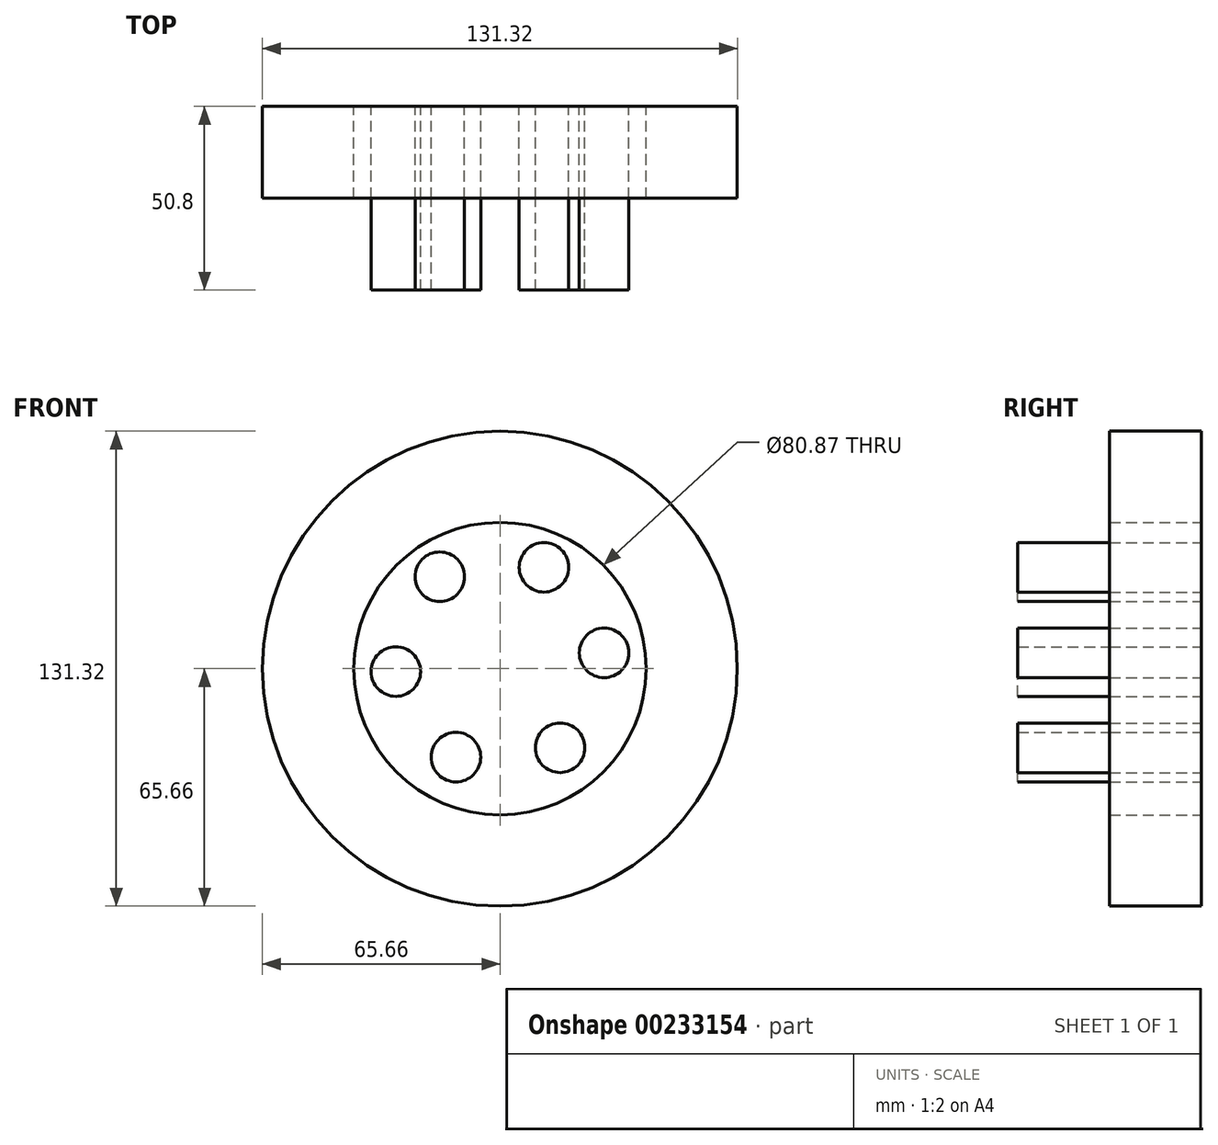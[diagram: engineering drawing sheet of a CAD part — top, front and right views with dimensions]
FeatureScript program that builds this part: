
annotation { "Feature Type Name" : "Feature", "Feature Type Description" : "" }
export const myFeature = defineFeature(function(context is Context, id is Id, definition is map)
    precondition{}
    {
        {
            var Q0;
            Q0=qCreatedBy(makeId("Front.planeOp"),FACE);
            var sketch = newSketch(context, id + "F0", { "sketchPlane" : qUnion([Q0])});
            skCircle(sketch, "E0", {"center": v(0, 0) * mm, "radius": 65.66 * mm});
            skCircle(sketch, "E1", {"center": v(0, 0) * mm, "radius": 40.44 * mm});
            skCircle(sketch, "E2", {"center": v(0, 27.91) * mm, "radius": 7.4 * mm});
            skCircle(sketch, "E3.1.0", {"center": v(-24.17, 13.96) * mm, "radius": 7.4 * mm});
            skCircle(sketch, "E3.2.0", {"center": v(-24.17, -13.96) * mm, "radius": 7.4 * mm});
            skCircle(sketch, "E3.3.0", {"center": v(0, -27.91) * mm, "radius": 7.4 * mm});
            skCircle(sketch, "E3.4.0", {"center": v(24.17, -13.96) * mm, "radius": 7.4 * mm});
            skCircle(sketch, "E3.5.0", {"center": v(24.17, 13.96) * mm, "radius": 7.4 * mm});
            skSolve(sketch);
        }
        {
            var Q0;
            Q0=qCreatedBy(makeId("Front.planeOp"),FACE);
            var sketch = newSketch(context, id + "F1", { "sketchPlane" : qUnion([Q0])});
            skCircle(sketch, "E4", {"center": v(0, 0) * mm, "radius": 67.87 * mm});
            skSolve(sketch);
        }
        {
            var Q0;
            Q0=sQuery(id+"F1.wireOp",EDGE,"E4");
            extrude(context, id + "F2", {"bodyType" : ToolBodyType.SURFACE, "surfaceEntities" : qUnion([Q0]), "depth" : 25.4 * mm});
        }
        {
            var Q0;
            Q0 = qSketchRegion(id + "F0", true);
            extrude(context, id + "F3", {"entities" : qUnion([Q0]), "depth" : 25.4 * mm});
        }
        {
            var Q0;
            Q0=qCreatedBy(makeId("Front.planeOp"),FACE);
            var sketch = newSketch(context, id + "F4", { "sketchPlane" : qUnion([Q0])});
            skCircle(sketch, "E5", {"center": v(-16.64, 25.43) * mm, "radius": 6.85 * mm});
            skCircle(sketch, "E6.1.0", {"center": v(-28.8, -0.8) * mm, "radius": 6.85 * mm});
            skCircle(sketch, "E6.2.0", {"center": v(-12.16, -24.46) * mm, "radius": 6.85 * mm});
            skCircle(sketch, "E6.3.0", {"center": v(16.64, -21.87) * mm, "radius": 6.85 * mm});
            skCircle(sketch, "E6.4.0", {"center": v(28.8, 4.37) * mm, "radius": 6.85 * mm});
            skCircle(sketch, "E6.5.0", {"center": v(12.16, 28.02) * mm, "radius": 6.85 * mm});
            skPoint(sketch, "E6.center", {"position": v(0, 1.78) * mm});
            skSolve(sketch);
        }
        {
            var Q0;
            Q0=makeQuery(id+"F4.imprint","IMPRINT",FACE,{"disambiguationData":[TD([[makeQuery(id+"F4.imprint","IMPRINT",EDGE,{"derivedFrom":sQuery(id+"F4.wireOp",EDGE,"E6.5.0")}),1.0]])]});
            var Q1;
            Q1=makeQuery(id+"F4.imprint","IMPRINT",FACE,{"disambiguationData":[TD([[makeQuery(id+"F4.imprint","IMPRINT",EDGE,{"derivedFrom":sQuery(id+"F4.wireOp",EDGE,"E5")}),1.0]])]});
            var Q2;
            Q2=makeQuery(id+"F4.imprint","IMPRINT",FACE,{"disambiguationData":[TD([[makeQuery(id+"F4.imprint","IMPRINT",EDGE,{"derivedFrom":sQuery(id+"F4.wireOp",EDGE,"E6.1.0")}),1.0]])]});
            var Q3;
            Q3=makeQuery(id+"F4.imprint","IMPRINT",FACE,{"disambiguationData":[TD([[makeQuery(id+"F4.imprint","IMPRINT",EDGE,{"derivedFrom":sQuery(id+"F4.wireOp",EDGE,"E6.2.0")}),1.0]])]});
            var Q4;
            Q4=makeQuery(id+"F4.imprint","IMPRINT",FACE,{"disambiguationData":[TD([[makeQuery(id+"F4.imprint","IMPRINT",EDGE,{"derivedFrom":sQuery(id+"F4.wireOp",EDGE,"E6.3.0")}),1.0]])]});
            var Q5;
            Q5=makeQuery(id+"F4.imprint","IMPRINT",FACE,{"disambiguationData":[TD([[makeQuery(id+"F4.imprint","IMPRINT",EDGE,{"derivedFrom":sQuery(id+"F4.wireOp",EDGE,"E6.4.0")}),1.0]])]});
            extrude(context, id + "F5", {"entities" : qUnion([Q0, Q1, Q2, Q3, Q4, Q5]), "depth" : 25.4 * mm});
        }
        {
            var Q0;
            Q0=makeQuery(id+"F5.opExtrude","CAP_FACE",FACE,{"disambiguationData":[OSD([sQuery(id+"F4.wireOp",EDGE,"E6.2.0")])],"isStart":false});
            var Q1;
            Q1=makeQuery(id+"F5.opExtrude","CAP_FACE",FACE,{"disambiguationData":[OSD([sQuery(id+"F4.wireOp",EDGE,"E6.3.0")])],"isStart":false});
            var Q2;
            Q2=makeQuery(id+"F5.opExtrude","CAP_FACE",FACE,{"disambiguationData":[OSD([sQuery(id+"F4.wireOp",EDGE,"E6.4.0")])],"isStart":false});
            var Q3;
            Q3=makeQuery(id+"F5.opExtrude","CAP_FACE",FACE,{"disambiguationData":[OSD([sQuery(id+"F4.wireOp",EDGE,"E6.1.0")])],"isStart":false});
            extrude(context, id + "F6", {"entities" : qUnion([Q0, Q1, Q2, Q3]), "depth" : 25.4 * mm});
        }
        {
            var Q0;
            Q0=makeQuery(id+"F5.opExtrude","CAP_FACE",FACE,{"disambiguationData":[OSD([sQuery(id+"F4.wireOp",EDGE,"E5")])],"isStart":false});
            extrude(context, id + "F7", {"entities" : qUnion([Q0]), "operationType" : NewBodyOperationType.ADD, "depth" : 25.4 * mm});
        }
        {
            var Q0;
            Q0=makeQuery(id+"F5.opExtrude","CAP_FACE",FACE,{"disambiguationData":[OSD([sQuery(id+"F4.wireOp",EDGE,"E6.5.0")])],"isStart":false});
            extrude(context, id + "F8", {"entities" : qUnion([Q0]), "operationType" : NewBodyOperationType.ADD, "depth" : 25.4 * mm});
        }
    });
